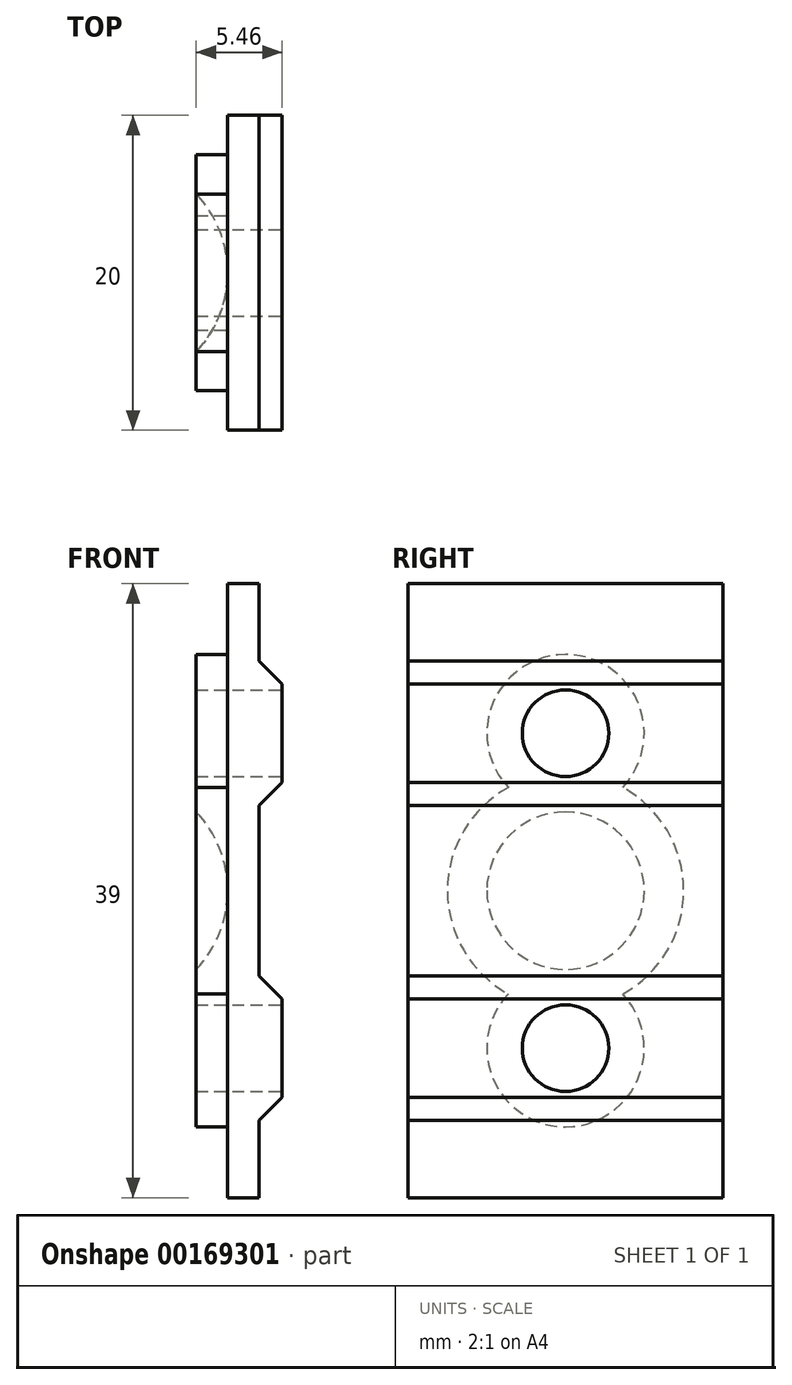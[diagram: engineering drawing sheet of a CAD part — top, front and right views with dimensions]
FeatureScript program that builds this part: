
annotation { "Feature Type Name" : "Feature", "Feature Type Description" : "" }
export const myFeature = defineFeature(function(context is Context, id is Id, definition is map)
    precondition{}
    {
        {
            var Q0;
            Q0=qCreatedBy(makeId("Front.planeOp"),FACE);
            var sketch = newSketch(context, id + "F0", { "sketchPlane" : qUnion([Q0])});
            skLineSegment(sketch, "E0.0.0", {"start": v(3.9, 10.2) * mm, "end": v(3.7, 10) * mm});
            skLineSegment(sketch, "E0.0.1", {"start": v(3.7, 10) * mm, "end": v(3.9, 9.79) * mm});
            skLineSegment(sketch, "E0.0.2", {"start": v(3.9, 9.79) * mm, "end": v(3.9, 7.16) * mm});
            skLineSegment(sketch, "E0.0.3", {"start": v(3.9, 7.16) * mm, "end": v(6.56, 4.5) * mm});
            skLineSegment(sketch, "E0.0.4", {"start": v(6.56, 4.5) * mm, "end": v(8.2, 4.5) * mm});
            skLineSegment(sketch, "E0.0.5", {"start": v(8.2, 4.5) * mm, "end": v(8.2, 6.87) * mm});
            skLineSegment(sketch, "E0.0.6", {"start": v(8.2, 6.87) * mm, "end": v(8.55, 6.87) * mm});
            skLineSegment(sketch, "E0.0.7", {"start": v(8.55, 6.87) * mm, "end": v(10, 5.42) * mm});
            skLineSegment(sketch, "E0.0.8", {"start": v(10, 5.42) * mm, "end": v(10, -5.42) * mm});
            skLineSegment(sketch, "E0.0.9", {"start": v(10, -5.42) * mm, "end": v(8.55, -6.88) * mm});
            skLineSegment(sketch, "E0.0.10", {"start": v(8.55, -6.88) * mm, "end": v(8.2, -6.88) * mm});
            skLineSegment(sketch, "E0.0.11", {"start": v(8.2, -6.88) * mm, "end": v(8.2, -4.5) * mm});
            skLineSegment(sketch, "E0.0.12", {"start": v(8.2, -4.5) * mm, "end": v(6.56, -4.5) * mm});
            skLineSegment(sketch, "E0.0.13", {"start": v(6.56, -4.5) * mm, "end": v(3.9, -7.16) * mm});
            skLineSegment(sketch, "E0.0.14", {"start": v(3.9, -7.16) * mm, "end": v(3.9, -9.8) * mm});
            skLineSegment(sketch, "E0.0.15", {"start": v(3.9, -9.8) * mm, "end": v(3.69, -10) * mm});
            skLineSegment(sketch, "E0.0.16", {"start": v(3.69, -10) * mm, "end": v(3.9, -10.21) * mm});
            skLineSegment(sketch, "E0.0.17", {"start": v(3.9, -10.21) * mm, "end": v(3.9, -12.84) * mm});
            skLineSegment(sketch, "E0.0.18", {"start": v(3.9, -12.84) * mm, "end": v(6.56, -15.5) * mm});
            skLineSegment(sketch, "E0.0.19", {"start": v(6.56, -15.5) * mm, "end": v(8.2, -15.5) * mm});
            skLineSegment(sketch, "E0.0.20", {"start": v(8.2, -15.5) * mm, "end": v(8.2, -13.13) * mm});
            skLineSegment(sketch, "E0.0.21", {"start": v(8.2, -13.13) * mm, "end": v(8.54, -13.13) * mm});
            skLineSegment(sketch, "E0.0.22", {"start": v(8.54, -13.13) * mm, "end": v(10, -14.58) * mm});
            skLineSegment(sketch, "E0.0.23", {"start": v(10, -14.58) * mm, "end": v(10, -19.5) * mm});
            skArc(sketch, "E0.0.24", {"start": v(10, -19.5) * mm, "mid": v(9.85, -19.85) * mm, "end": v(9.5, -20) * mm});
            skLineSegment(sketch, "E0.0.25", {"start": v(9.5, -20) * mm, "end": v(4.58, -20) * mm});
            skLineSegment(sketch, "E0.0.26", {"start": v(4.58, -20) * mm, "end": v(3.12, -18.55) * mm});
            skLineSegment(sketch, "E0.0.27", {"start": v(3.12, -18.55) * mm, "end": v(3.12, -18.2) * mm});
            skLineSegment(sketch, "E0.0.28", {"start": v(3.12, -18.2) * mm, "end": v(5.5, -18.2) * mm});
            skLineSegment(sketch, "E0.0.29", {"start": v(5.5, -18.2) * mm, "end": v(5.5, -16.56) * mm});
            skLineSegment(sketch, "E0.0.30", {"start": v(5.5, -16.56) * mm, "end": v(2.84, -13.9) * mm});
            skLineSegment(sketch, "E0.0.31", {"start": v(2.84, -13.9) * mm, "end": v(0.2, -13.9) * mm});
            skLineSegment(sketch, "E0.0.32", {"start": v(0.2, -13.9) * mm, "end": v(0, -13.7) * mm});
            skLineSegment(sketch, "E0.0.33", {"start": v(0, -13.7) * mm, "end": v(-0.21, -13.9) * mm});
            skLineSegment(sketch, "E0.0.34", {"start": v(-0.21, -13.9) * mm, "end": v(-2.84, -13.9) * mm});
            skLineSegment(sketch, "E0.0.35", {"start": v(-2.84, -13.9) * mm, "end": v(-5.5, -16.56) * mm});
            skLineSegment(sketch, "E0.0.36", {"start": v(-5.5, -16.56) * mm, "end": v(-5.5, -18.2) * mm});
            skLineSegment(sketch, "E0.0.37", {"start": v(-5.5, -18.2) * mm, "end": v(-3.13, -18.2) * mm});
            skLineSegment(sketch, "E0.0.38", {"start": v(-3.13, -18.2) * mm, "end": v(-3.13, -18.55) * mm});
            skLineSegment(sketch, "E0.0.39", {"start": v(-3.13, -18.55) * mm, "end": v(-4.58, -20) * mm});
            skLineSegment(sketch, "E0.0.40", {"start": v(-4.58, -20) * mm, "end": v(-9.5, -20) * mm});
            skArc(sketch, "E0.0.41", {"start": v(-9.5, -20) * mm, "mid": v(-9.85, -19.85) * mm, "end": v(-10, -19.5) * mm});
            skLineSegment(sketch, "E0.0.42", {"start": v(-10, -19.5) * mm, "end": v(-10, -14.58) * mm});
            skLineSegment(sketch, "E0.0.43", {"start": v(-10, -14.58) * mm, "end": v(-8.55, -13.13) * mm});
            skLineSegment(sketch, "E0.0.44", {"start": v(-8.55, -13.13) * mm, "end": v(-8.2, -13.13) * mm});
            skLineSegment(sketch, "E0.0.45", {"start": v(-8.2, -13.13) * mm, "end": v(-8.2, -15.5) * mm});
            skLineSegment(sketch, "E0.0.46", {"start": v(-8.2, -15.5) * mm, "end": v(-6.56, -15.5) * mm});
            skLineSegment(sketch, "E0.0.47", {"start": v(-6.56, -15.5) * mm, "end": v(-3.9, -12.84) * mm});
            skLineSegment(sketch, "E0.0.48", {"start": v(-3.9, -12.84) * mm, "end": v(-3.9, -10.2) * mm});
            skLineSegment(sketch, "E0.0.49", {"start": v(-3.9, -10.2) * mm, "end": v(-3.7, -10) * mm});
            skLineSegment(sketch, "E0.0.50", {"start": v(-3.7, -10) * mm, "end": v(-3.9, -9.79) * mm});
            skLineSegment(sketch, "E0.0.51", {"start": v(-3.9, -9.79) * mm, "end": v(-3.9, -7.16) * mm});
            skLineSegment(sketch, "E0.0.52", {"start": v(-3.9, -7.16) * mm, "end": v(-6.56, -4.5) * mm});
            skLineSegment(sketch, "E0.0.53", {"start": v(-6.56, -4.5) * mm, "end": v(-8.2, -4.5) * mm});
            skLineSegment(sketch, "E0.0.54", {"start": v(-8.2, -4.5) * mm, "end": v(-8.2, -6.87) * mm});
            skLineSegment(sketch, "E0.0.55", {"start": v(-8.2, -6.87) * mm, "end": v(-8.55, -6.87) * mm});
            skLineSegment(sketch, "E0.0.56", {"start": v(-8.55, -6.87) * mm, "end": v(-10, -5.42) * mm});
            skLineSegment(sketch, "E0.0.57", {"start": v(-10, -5.42) * mm, "end": v(-10, 5.42) * mm});
            skLineSegment(sketch, "E0.0.58", {"start": v(-10, 5.42) * mm, "end": v(-8.55, 6.88) * mm});
            skLineSegment(sketch, "E0.0.59", {"start": v(-8.55, 6.88) * mm, "end": v(-8.2, 6.88) * mm});
            skLineSegment(sketch, "E0.0.60", {"start": v(-8.2, 6.88) * mm, "end": v(-8.2, 4.5) * mm});
            skLineSegment(sketch, "E0.0.61", {"start": v(-8.2, 4.5) * mm, "end": v(-6.56, 4.5) * mm});
            skLineSegment(sketch, "E0.0.62", {"start": v(-6.56, 4.5) * mm, "end": v(-3.9, 7.16) * mm});
            skLineSegment(sketch, "E0.0.63", {"start": v(-3.9, 7.16) * mm, "end": v(-3.9, 9.8) * mm});
            skLineSegment(sketch, "E0.0.64", {"start": v(-3.9, 9.8) * mm, "end": v(-3.7, 10) * mm});
            skLineSegment(sketch, "E0.0.65", {"start": v(-3.7, 10) * mm, "end": v(-3.9, 10.21) * mm});
            skLineSegment(sketch, "E0.0.66", {"start": v(-3.9, 10.21) * mm, "end": v(-3.9, 12.84) * mm});
            skLineSegment(sketch, "E0.0.67", {"start": v(-3.9, 12.84) * mm, "end": v(-6.56, 15.5) * mm});
            skLineSegment(sketch, "E0.0.68", {"start": v(-6.56, 15.5) * mm, "end": v(-8.2, 15.5) * mm});
            skLineSegment(sketch, "E0.0.69", {"start": v(-8.2, 15.5) * mm, "end": v(-8.2, 13.13) * mm});
            skLineSegment(sketch, "E0.0.70", {"start": v(-8.2, 13.13) * mm, "end": v(-8.55, 13.13) * mm});
            skLineSegment(sketch, "E0.0.71", {"start": v(-8.55, 13.13) * mm, "end": v(-10, 14.58) * mm});
            skLineSegment(sketch, "E0.0.72", {"start": v(-10, 14.58) * mm, "end": v(-10, 19.5) * mm});
            skArc(sketch, "E0.0.73", {"start": v(-10, 19.5) * mm, "mid": v(-9.85, 19.85) * mm, "end": v(-9.5, 20) * mm});
            skLineSegment(sketch, "E0.0.74", {"start": v(-9.5, 20) * mm, "end": v(-4.58, 20) * mm});
            skLineSegment(sketch, "E0.0.75", {"start": v(-4.58, 20) * mm, "end": v(-3.12, 18.55) * mm});
            skLineSegment(sketch, "E0.0.76", {"start": v(-3.12, 18.55) * mm, "end": v(-3.12, 18.2) * mm});
            skLineSegment(sketch, "E0.0.77", {"start": v(-3.12, 18.2) * mm, "end": v(-5.5, 18.2) * mm});
            skLineSegment(sketch, "E0.0.78", {"start": v(-5.5, 18.2) * mm, "end": v(-5.5, 16.56) * mm});
            skLineSegment(sketch, "E0.0.79", {"start": v(-5.5, 16.56) * mm, "end": v(-2.84, 13.9) * mm});
            skLineSegment(sketch, "E0.0.80", {"start": v(-2.84, 13.9) * mm, "end": v(-0.2, 13.9) * mm});
            skLineSegment(sketch, "E0.0.81", {"start": v(-0.2, 13.9) * mm, "end": v(0, 13.69) * mm});
            skLineSegment(sketch, "E0.0.82", {"start": v(0, 13.69) * mm, "end": v(0.21, 13.9) * mm});
            skLineSegment(sketch, "E0.0.83", {"start": v(0.21, 13.9) * mm, "end": v(2.84, 13.9) * mm});
            skLineSegment(sketch, "E0.0.84", {"start": v(2.84, 13.9) * mm, "end": v(5.5, 16.56) * mm});
            skLineSegment(sketch, "E0.0.85", {"start": v(5.5, 16.56) * mm, "end": v(5.5, 18.2) * mm});
            skLineSegment(sketch, "E0.0.86", {"start": v(5.5, 18.2) * mm, "end": v(3.13, 18.2) * mm});
            skLineSegment(sketch, "E0.0.87", {"start": v(3.13, 18.2) * mm, "end": v(3.13, 18.54) * mm});
            skLineSegment(sketch, "E0.0.88", {"start": v(3.13, 18.54) * mm, "end": v(4.58, 20) * mm});
            skLineSegment(sketch, "E0.0.89", {"start": v(4.58, 20) * mm, "end": v(9.5, 20) * mm});
            skArc(sketch, "E0.0.90", {"start": v(9.5, 20) * mm, "mid": v(9.85, 19.85) * mm, "end": v(10, 19.5) * mm});
            skLineSegment(sketch, "E0.0.91", {"start": v(10, 19.5) * mm, "end": v(10, 14.58) * mm});
            skLineSegment(sketch, "E0.0.92", {"start": v(10, 14.58) * mm, "end": v(8.55, 13.12) * mm});
            skLineSegment(sketch, "E0.0.93", {"start": v(8.55, 13.12) * mm, "end": v(8.2, 13.12) * mm});
            skLineSegment(sketch, "E0.0.94", {"start": v(8.2, 13.12) * mm, "end": v(8.2, 15.5) * mm});
            skLineSegment(sketch, "E0.0.95", {"start": v(8.2, 15.5) * mm, "end": v(6.56, 15.5) * mm});
            skLineSegment(sketch, "E0.0.96", {"start": v(6.56, 15.5) * mm, "end": v(3.9, 12.84) * mm});
            skLineSegment(sketch, "E0.0.97", {"start": v(3.9, 12.84) * mm, "end": v(3.9, 10.2) * mm});
            skLineSegment(sketch, "E1.0.0", {"start": v(-6.24, -2.7) * mm, "end": v(-8.2, -2.7) * mm});
            skLineSegment(sketch, "E1.0.1", {"start": v(-8.2, -2.7) * mm, "end": v(-8.2, 2.7) * mm});
            skLineSegment(sketch, "E1.0.2", {"start": v(-8.2, 2.7) * mm, "end": v(-6.24, 2.7) * mm});
            skLineSegment(sketch, "E1.0.3", {"start": v(-6.24, 2.7) * mm, "end": v(-2.84, 6.1) * mm});
            skLineSegment(sketch, "E1.0.4", {"start": v(-2.84, 6.1) * mm, "end": v(2.84, 6.1) * mm});
            skLineSegment(sketch, "E1.0.5", {"start": v(2.84, 6.1) * mm, "end": v(6.24, 2.7) * mm});
            skLineSegment(sketch, "E1.0.6", {"start": v(6.24, 2.7) * mm, "end": v(8.2, 2.7) * mm});
            skLineSegment(sketch, "E1.0.7", {"start": v(8.2, 2.7) * mm, "end": v(8.2, -2.7) * mm});
            skLineSegment(sketch, "E1.0.8", {"start": v(8.2, -2.7) * mm, "end": v(6.24, -2.7) * mm});
            skLineSegment(sketch, "E1.0.9", {"start": v(6.24, -2.7) * mm, "end": v(2.84, -6.1) * mm});
            skLineSegment(sketch, "E1.0.10", {"start": v(2.84, -6.1) * mm, "end": v(-2.84, -6.1) * mm});
            skLineSegment(sketch, "E1.0.11", {"start": v(-2.84, -6.1) * mm, "end": v(-6.24, -2.7) * mm});
            skSolve(sketch);
        }
        {
            var Q0;
            Q0=qCreatedBy(makeId("Front.planeOp"),FACE);
            var sketch = newSketch(context, id + "F1", { "sketchPlane" : qUnion([Q0])});
            skLineSegment(sketch, "E2.0", {"start": v(-10, 5.42) * mm, "end": v(-8.55, 6.88) * mm});
            skLineSegment(sketch, "E3.0", {"start": v(-8.55, 13.13) * mm, "end": v(-10, 14.58) * mm});
            skLineSegment(sketch, "E4.0", {"start": v(-8.55, -6.87) * mm, "end": v(-10, -5.42) * mm});
            skLineSegment(sketch, "E5.0", {"start": v(-10, -14.58) * mm, "end": v(-8.55, -13.13) * mm});
            skLineSegment(sketch, "E6.0", {"start": v(-10, -19.5) * mm, "end": v(-10, -14.58) * mm});
            skLineSegment(sketch, "E7.0", {"start": v(-10, -5.42) * mm, "end": v(-10, 5.42) * mm});
            skLineSegment(sketch, "E8.0", {"start": v(-10, 14.58) * mm, "end": v(-10, 19.5) * mm});
            skLineSegment(sketch, "E9", {"start": v(-8.55, 13.13) * mm, "end": v(-8.55, 6.88) * mm});
            skLineSegment(sketch, "E10", {"start": v(-8.55, -6.87) * mm, "end": v(-8.55, -13.13) * mm});
            skLineSegment(sketch, "E11", {"start": v(-10, -19.5) * mm, "end": v(-12, -19.5) * mm});
            skLineSegment(sketch, "E12", {"start": v(-12, -19.5) * mm, "end": v(-12, 19.5) * mm});
            skLineSegment(sketch, "E13", {"start": v(-12, 19.5) * mm, "end": v(-10, 19.5) * mm});
            skSolve(sketch);
        }
        {
            var Q0;
            Q0 = qSketchRegion(id + "F1", true);
            extrude(context, id + "F2", {"entities" : qUnion([Q0]), "depth" : 20 * mm, "symmetric" : true});
        }
        {
            var Q0;
            Q0=makeQuery(id+"F2.opExtrude","SWEPT_FACE",FACE,{"disambiguationData":[OSD([sQuery(id+"F1.wireOp",EDGE,"E12")])]});
            var sketch = newSketch(context, id + "F3", { "sketchPlane" : qUnion([Q0])});
            skLineSegment(sketch, "E14", {"start": v(-10, 19.5) * mm, "end": v(10, -19.5) * mm, "construction": true});
            skPoint(sketch, "E15.endSnap0", {"position": v(0, 0) * mm});
            skPoint(sketch, "E15.start.orphan", {"position": v(0, 0) * mm});
            skCircle(sketch, "E16", {"center": v(0, 0) * mm, "radius": 7.5 * mm});
            skSolve(sketch);
        }
        {
            var Q0;
            Q0 = qSketchRegion(id + "F3", true);
            extrude(context, id + "F4", {"entities" : qUnion([Q0]), "operationType" : NewBodyOperationType.ADD, "depth" : 2 * mm});
        }
        {
            var Q0;
            Q0=qCreatedBy(makeId("Top.planeOp"),FACE);
            var sketch = newSketch(context, id + "F5", { "sketchPlane" : qUnion([Q0])});
            skArc(sketch, "E17", {"start": v(-14, -5) * mm, "mid": v(-12.52, -2.7) * mm, "end": v(-12, 0) * mm});
            skPoint(sketch, "E18", {"position": v(-14, -7.5) * mm});
            skPoint(sketch, "E19", {"position": v(-14, 7.5) * mm});
            skLineSegment(sketch, "E20", {"start": v(-14, 7.5) * mm, "end": v(-14, 5) * mm, "construction": true});
            skLineSegment(sketch, "E21", {"start": v(-14, -5) * mm, "end": v(-14, -7.5) * mm, "construction": true});
            skLineSegment(sketch, "E22", {"start": v(-12, 0) * mm, "end": v(-14, 0) * mm});
            skPoint(sketch, "E22.endSnap0", {"position": v(-12, 0) * mm});
            skLineSegment(sketch, "E23", {"start": v(-14, 0) * mm, "end": v(-14, -5) * mm});
            skSolve(sketch);
        }
        {
            var Q0;
            Q0 = qSketchRegion(id + "F5", true);
            var Q1;
            Q1=sQuery(id+"F5.wireOp",EDGE,"E22");
            revolve(context, id + "F6", {"operationType" : NewBodyOperationType.REMOVE, "entities" : qUnion([Q0]), "axis" : qUnion([Q1]), "revolveType" : RevolveType.FULL, "oppositeDirection" : true});
        }
        {
            var Q0;
            Q0=makeQuery(id+"F2.opExtrude","SWEPT_FACE",FACE,{"disambiguationData":[OSD([sQuery(id+"F1.wireOp",EDGE,"E12")])]});
            var sketch = newSketch(context, id + "F7", { "sketchPlane" : qUnion([Q0])});
            skPoint(sketch, "E24", {"position": v(0, 10) * mm});
            skPoint(sketch, "E25", {"position": v(0, -10) * mm});
            skSolve(sketch);
        }
        {
            var Q0;
            Q0=sQuery(id+"F7.wireOp",VERTEX,"E24");
            var Q1;
            Q1=sQuery(id+"F7.wireOp",VERTEX,"E25");
            var Q2;
            Q2=makeQuery(id+"F2.opExtrude","SWEPT_BODY",BODY,{"disambiguationData":[OSD([sQuery(id+"F1.wireOp",EDGE,"E2.0"),sQuery(id+"F1.wireOp",EDGE,"E3.0"),sQuery(id+"F1.wireOp",EDGE,"E4.0"),sQuery(id+"F1.wireOp",EDGE,"E5.0"),sQuery(id+"F1.wireOp",EDGE,"E6.0"),sQuery(id+"F1.wireOp",EDGE,"E7.0"),sQuery(id+"F1.wireOp",EDGE,"E8.0"),sQuery(id+"F1.wireOp",EDGE,"E9"),sQuery(id+"F1.wireOp",EDGE,"E10"),sQuery(id+"F1.wireOp",EDGE,"E11"),sQuery(id+"F1.wireOp",EDGE,"E12"),sQuery(id+"F1.wireOp",EDGE,"E13")])]});
            hole(context, id + "F8", {"style" : HoleStyle.SIMPLE, "endStyle" : HoleEndStyle.THROUGH, "holeDiameter" : 5.5 * mm, "locations" : qUnion([Q0, Q1]), "scope" : qUnion([Q2]), "isTappedThrough" : true, "startStyle" : HoleStartStyle.PART});
        }
        {
            var Q0;
            Q0=makeQuery(id+"F2.opExtrude","SWEPT_FACE",FACE,{"disambiguationData":[OSD([sQuery(id+"F1.wireOp",EDGE,"E9")])]});
            var sketch = newSketch(context, id + "F9", { "sketchPlane" : qUnion([Q0])});
            skCircle(sketch, "E26.0", {"center": v(0, 10) * mm, "radius": 2.75 * mm});
            skCircle(sketch, "E27.0", {"center": v(0, -10) * mm, "radius": 2.75 * mm});
            skSolve(sketch);
        }
        {
            var Q0;
            Q0 = qSketchRegion(id + "F9", true);
            extrude(context, id + "F10", {"entities" : qUnion([Q0]), "operationType" : NewBodyOperationType.REMOVE, "oppositeDirection" : true, "depth" : 25 * mm});
        }
        {
            var Q0;
            Q0=makeQuery(id+"F2.opExtrude","SWEPT_FACE",FACE,{"disambiguationData":[OSD([sQuery(id+"F1.wireOp",EDGE,"E12")])]});
            var sketch = newSketch(context, id + "F11", { "sketchPlane" : qUnion([Q0])});
            skCircle(sketch, "E28.0", {"center": v(0, 10) * mm, "radius": 2.75 * mm});
            skCircle(sketch, "E29.0", {"center": v(0, -10) * mm, "radius": 2.75 * mm});
            skCircle(sketch, "E30", {"center": v(0, 10) * mm, "radius": 5 * mm});
            skCircle(sketch, "E31", {"center": v(0, -10) * mm, "radius": 5 * mm});
            skSolve(sketch);
        }
        {
            var Q0;
            Q0 = qSketchRegion(id + "F11", true);
            var Q1;
            Q1=makeQuery(id+"F4.opExtrude","CAP_FACE",FACE,{"disambiguationData":[OSD([sQuery(id+"F3.wireOp",EDGE,"E16")])],"isStart":false});
            extrude(context, id + "F12", {"entities" : qUnion([Q0]), "operationType" : NewBodyOperationType.ADD, "endBound" : BoundingType.UP_TO_SURFACE, "endBoundEntityFace" : qUnion([Q1]), "depth" : 25 * mm});
        }
    });
